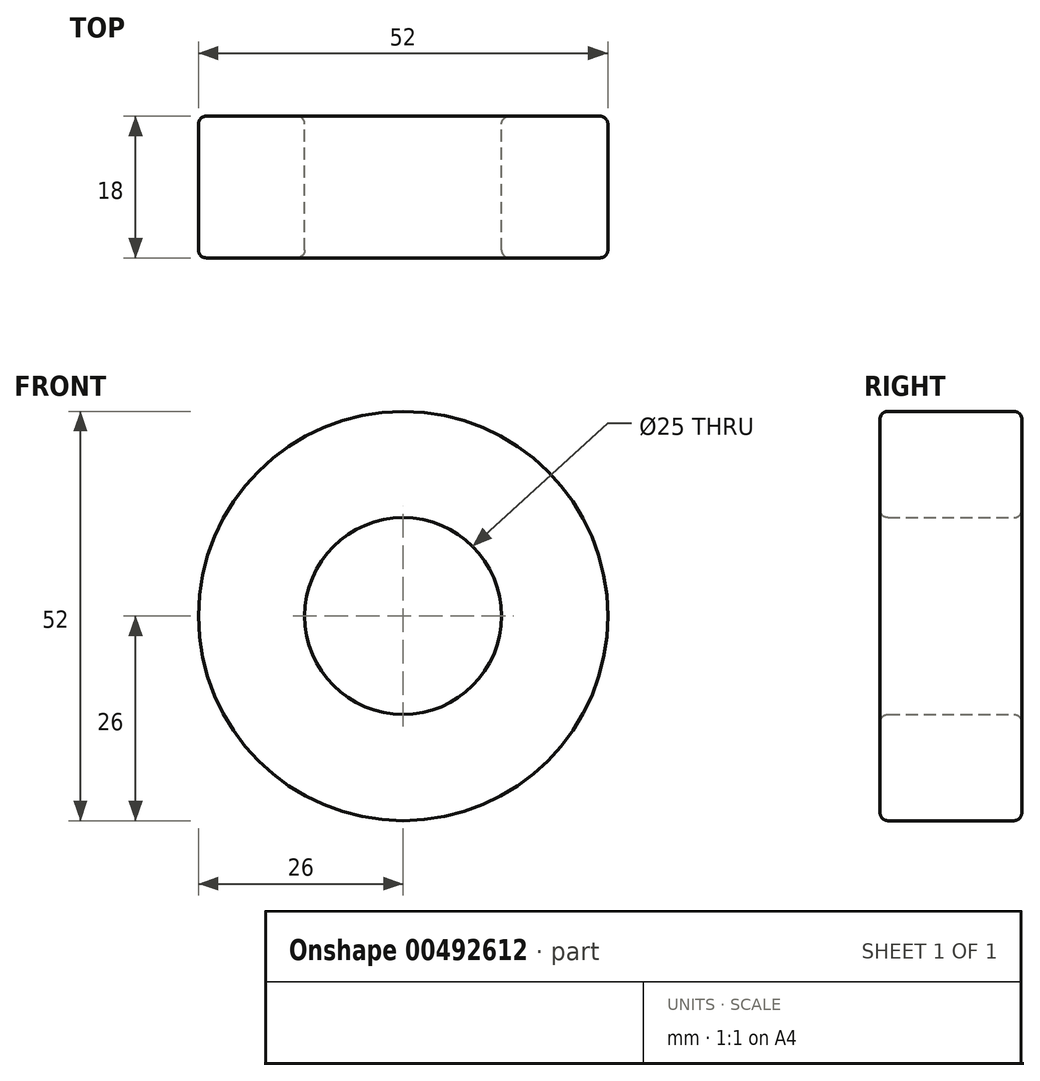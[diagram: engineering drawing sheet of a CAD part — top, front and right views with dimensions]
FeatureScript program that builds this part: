
annotation { "Feature Type Name" : "Feature", "Feature Type Description" : "" }
export const myFeature = defineFeature(function(context is Context, id is Id, definition is map)
    precondition{}
    {
        {
            var Q0;
            Q0=qCreatedBy(makeId("Front.planeOp"),FACE);
            var sketch = newSketch(context, id + "F0", { "sketchPlane" : qUnion([Q0])});
            skCircle(sketch, "E0", {"center": v(0, 0) * mm, "radius": 26 * mm});
            skCircle(sketch, "E1", {"center": v(0, 0) * mm, "radius": 12.5 * mm});
            skSolve(sketch);
        }
        {
            var Q0;
            Q0=makeQuery(id+"F0.imprint","IMPRINT",FACE,{"disambiguationData":[TD([[makeQuery(id+"F0.imprint","IMPRINT",EDGE,{"derivedFrom":sQuery(id+"F0.wireOp",EDGE,"E0")}),1.0]])]});
            extrude(context, id + "F1", {"entities" : qUnion([Q0]), "offsetDistance" : 25 * mm, "depth" : 18 * mm});
        }
        {
            var Q0;
            Q0=makeQuery(id+"F1.opExtrude","CAP_EDGE",EDGE,{"disambiguationData":[OSD([sQuery(id+"F0.wireOp",EDGE,"E0")])],"isStart":false});
            var Q1;
            Q1=makeQuery(id+"F1.opExtrude","CAP_EDGE",EDGE,{"disambiguationData":[OSD([sQuery(id+"F0.wireOp",EDGE,"E0")])],"isStart":true});
            fillet(context, id + "F2", {"entities" : qUnion([Q0, Q1]), "radius" : 1 * mm, "tangentPropagation" : true, "allowEdgeOverflow" : false});
        }
        {
            var Q0;
            Q0=makeQuery(id+"F1.opExtrude","CAP_EDGE",EDGE,{"disambiguationData":[OSD([sQuery(id+"F0.wireOp",EDGE,"E1")])],"isStart":false});
            var Q1;
            Q1=makeQuery(id+"F1.opExtrude","CAP_EDGE",EDGE,{"disambiguationData":[OSD([sQuery(id+"F0.wireOp",EDGE,"E1")])],"isStart":true});
            fillet(context, id + "F3", {"entities" : qUnion([Q0, Q1]), "radius" : 1 * mm, "tangentPropagation" : true, "allowEdgeOverflow" : false});
        }
    });
